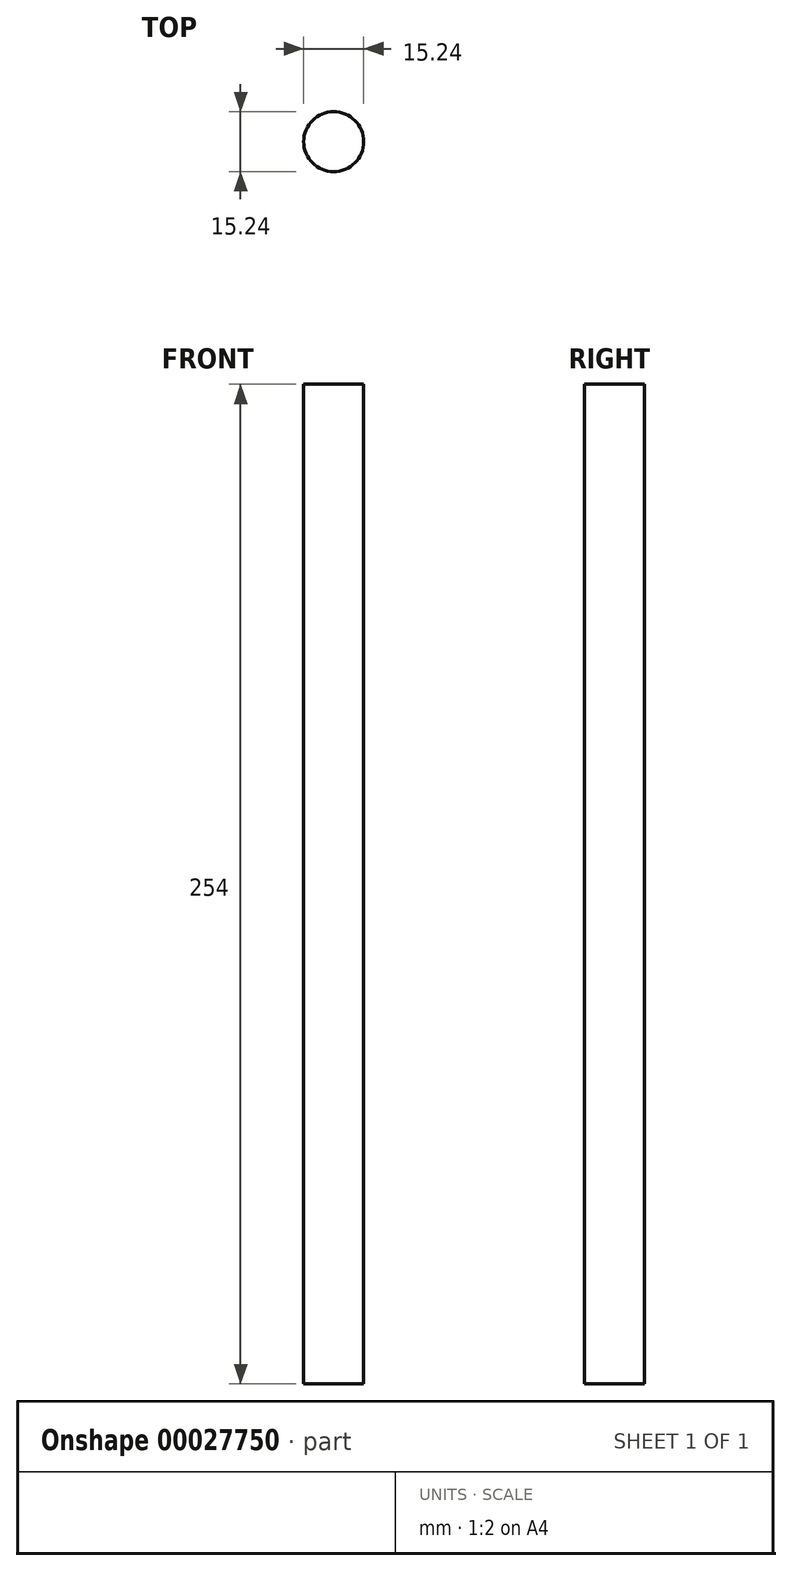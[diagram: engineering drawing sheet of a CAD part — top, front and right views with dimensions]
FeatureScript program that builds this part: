
annotation { "Feature Type Name" : "Feature", "Feature Type Description" : "" }
export const myFeature = defineFeature(function(context is Context, id is Id, definition is map)
    precondition{}
    {
        {
            var Q0;
            Q0=qCreatedBy(makeId("Top.planeOp"),FACE);
            var sketch = newSketch(context, id + "F0", { "sketchPlane" : qUnion([Q0])});
            skCircle(sketch, "E0", {"center": v(0, 0) * mm, "radius": 7.62 * mm});
            skSolve(sketch);
        }
        {
            var Q0;
            Q0=makeQuery(id+"F0.imprint","IMPRINT",FACE,{"disambiguationData":[TD([[makeQuery(id+"F0.imprint","IMPRINT",EDGE,{"derivedFrom":sQuery(id+"F0.wireOp",EDGE,"E0")}),1.0]])]});
            extrude(context, id + "F1", {"entities" : qUnion([Q0]), "depth" : 254 * mm});
        }
    });
